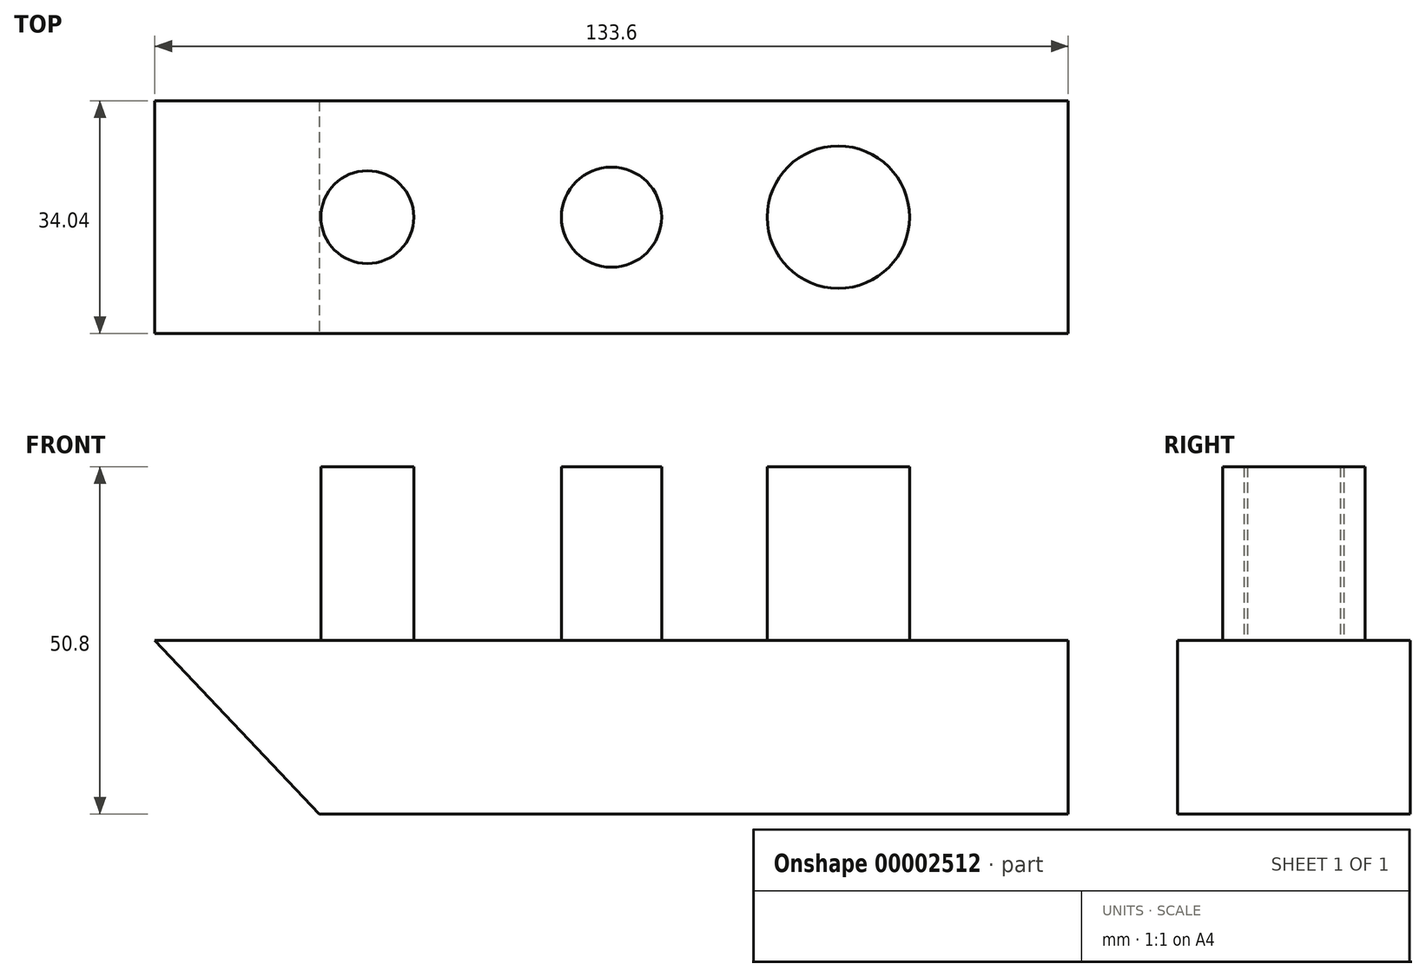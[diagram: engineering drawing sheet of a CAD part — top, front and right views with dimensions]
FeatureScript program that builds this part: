
annotation { "Feature Type Name" : "Feature", "Feature Type Description" : "" }
export const myFeature = defineFeature(function(context is Context, id is Id, definition is map)
    precondition{}
    {
        {
            var Q0;
            Q0=qCreatedBy(makeId("Top.planeOp"),FACE);
            var sketch = newSketch(context, id + "F0", { "sketchPlane" : qUnion([Q0])});
            skLineSegment(sketch, "E0.bottom", {"start": v(66.8, -17.02) * mm, "end": v(-66.8, -17.02) * mm});
            skLineSegment(sketch, "E0.top", {"start": v(66.8, 17.02) * mm, "end": v(-66.8, 17.02) * mm});
            skLineSegment(sketch, "E0.left", {"start": v(66.8, -17.02) * mm, "end": v(66.8, 17.02) * mm});
            skLineSegment(sketch, "E0.right", {"start": v(-66.8, -17.02) * mm, "end": v(-66.8, 17.02) * mm});
            skPoint(sketch, "E0.middle", {"position": v(0, 0) * mm});
            skSolve(sketch);
        }
        {
            var Q0;
            Q0 = qSketchRegion(id + "F0", true);
            extrude(context, id + "F1", {"entities" : qUnion([Q0]), "depth" : 25.4 * mm});
        }
        {
            var Q0;
            Q0=makeQuery(id+"F1.opExtrude","CAP_FACE",FACE,{"disambiguationData":[OSD([sQuery(id+"F0.wireOp",EDGE,"E0.bottom"),sQuery(id+"F0.wireOp",EDGE,"E0.top"),sQuery(id+"F0.wireOp",EDGE,"E0.left"),sQuery(id+"F0.wireOp",EDGE,"E0.right")])],"isStart":false});
            var sketch = newSketch(context, id + "F2", { "sketchPlane" : qUnion([Q0])});
            skCircle(sketch, "E1", {"center": v(0, 0) * mm, "radius": 7.32 * mm});
            skCircle(sketch, "E2", {"center": v(33.18, 0) * mm, "radius": 10.4 * mm});
            skCircle(sketch, "E3", {"center": v(-35.71, 0) * mm, "radius": 6.79 * mm});
            skSolve(sketch);
        }
        {
            var Q0;
            Q0 = qSketchRegion(id + "F2", true);
            extrude(context, id + "F3", {"entities" : qUnion([Q0]), "operationType" : NewBodyOperationType.ADD, "depth" : 25.4 * mm});
        }
        {
            var Q0;
            Q0=makeQuery(id+"F1.opExtrude","SWEPT_FACE",FACE,{"disambiguationData":[OSD([sQuery(id+"F0.wireOp",EDGE,"E0.bottom")])]});
            var sketch = newSketch(context, id + "F4", { "sketchPlane" : qUnion([Q0])});
            skLineSegment(sketch, "E4", {"start": v(-66.8, 25.4) * mm, "end": v(-42.73, 0) * mm});
            skLineSegment(sketch, "E5", {"start": v(-42.73, 0) * mm, "end": v(-66.8, 0) * mm});
            skLineSegment(sketch, "E6", {"start": v(-66.8, 0) * mm, "end": v(-66.8, 25.4) * mm});
            skSolve(sketch);
        }
        {
            var Q0;
            Q0 = qSketchRegion(id + "F4", true);
            extrude(context, id + "F5", {"entities" : qUnion([Q0]), "operationType" : NewBodyOperationType.REMOVE, "endBound" : BoundingType.THROUGH_ALL, "oppositeDirection" : true, "depth" : 25.4 * mm});
        }
    });
